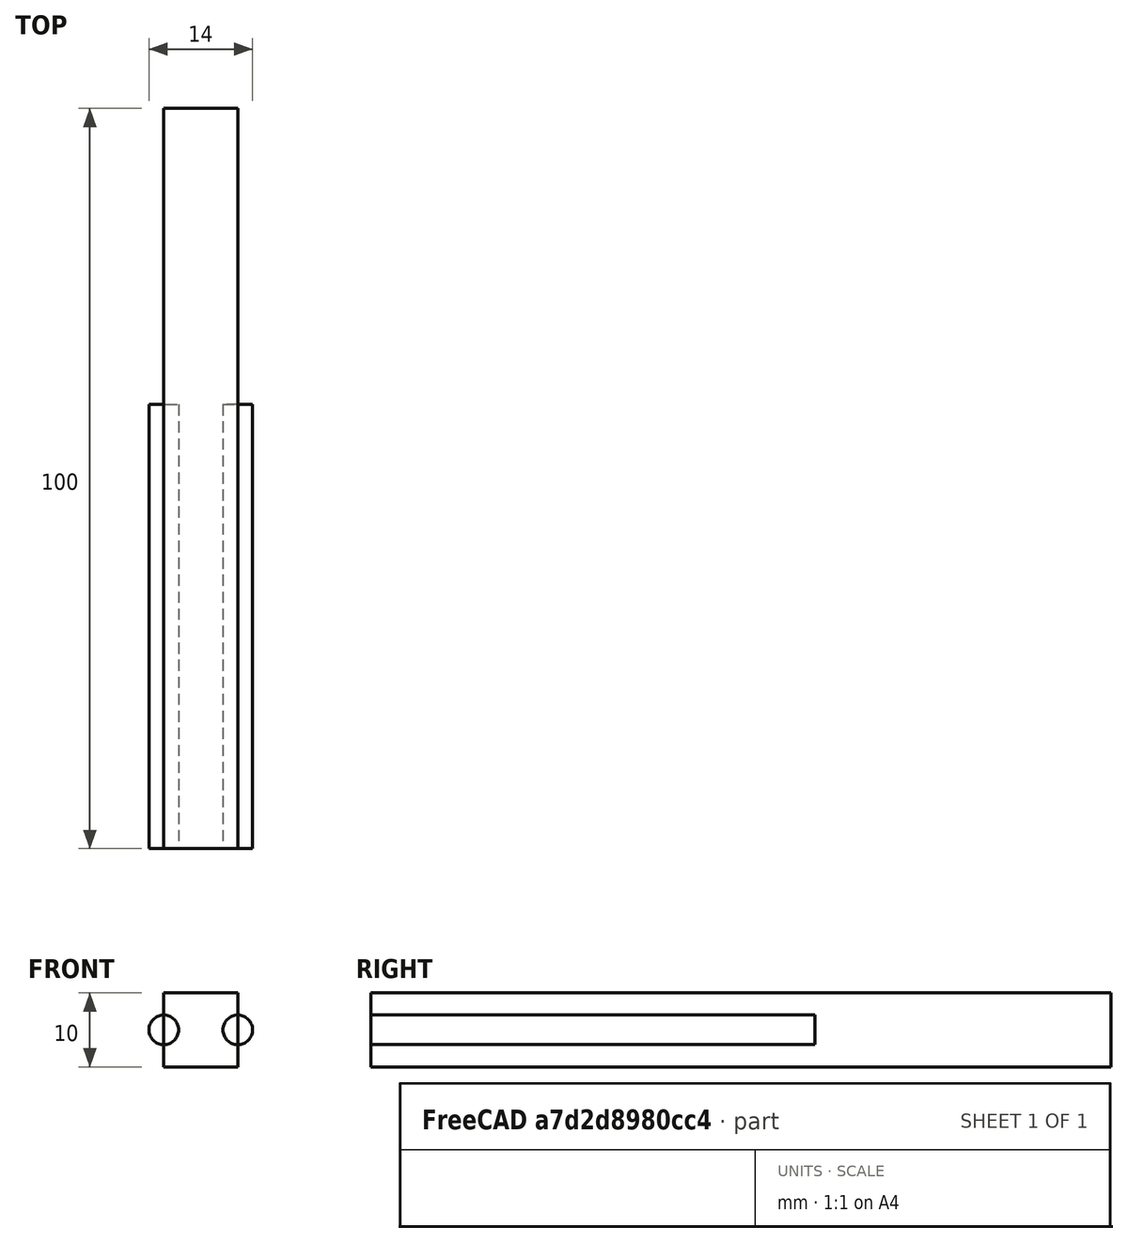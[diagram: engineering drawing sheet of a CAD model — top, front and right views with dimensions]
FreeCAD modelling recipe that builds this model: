
FCSTD DOCUMENT  (FreeCAD 0.14R3692 (Git))
Label: actuator3
License: CC-BY 3.0
LicenseURL: http://creativecommons.org/licenses/by/3.0/
objects: Part::Cylinder×4, Part::Box×2, Part::Cut×2
note: 8 computed .brp shape members not serialized (recipe doc carries the construction recipe); baked Part::Feature solids carry a one-line shape summary decoded from their .brp

FEATURE [Part::Box] Box  label="Cube"
  Height = 10
  Length = 10
  Placement = pos=(-5,0,-5) rot=(0,0,1;0rad)
  Width = 100
FEATURE [Part::Cylinder] Cylinder
  Angle = 360
  Height = 60
  Placement = pos=(-5,60,0) rot=(1,0,0;1.5708rad)
  Radius = 2
FEATURE [Part::Cylinder] Cylinder001
  Angle = 360
  Height = 60
  Placement = pos=(5,60,0) rot=(1,0,0;1.5708rad)
  Radius = 2
FEATURE [Part::Cylinder] Cylinder002
  Angle = 360
  Height = 60
  Placement = pos=(-5,60,0) rot=(1,0,0;1.5708rad)
  Radius = 2
FEATURE [Part::Cylinder] Cylinder003
  Angle = 360
  Height = 60
  Placement = pos=(5,60,0) rot=(1,0,0;1.5708rad)
  Radius = 2
FEATURE [Part::Cut] Cut
  Base = -> Box
  Tool = -> Cylinder
FEATURE [Part::Cut] Cut001
  Base = -> Cut
  Tool = -> Cylinder001
FEATURE [Part::Box] Box001  label="Cube001"
  Height = 10
  Length = 10
  Placement = pos=(-5,0,-5) rot=(0,0,1;0rad)
  Width = 100
